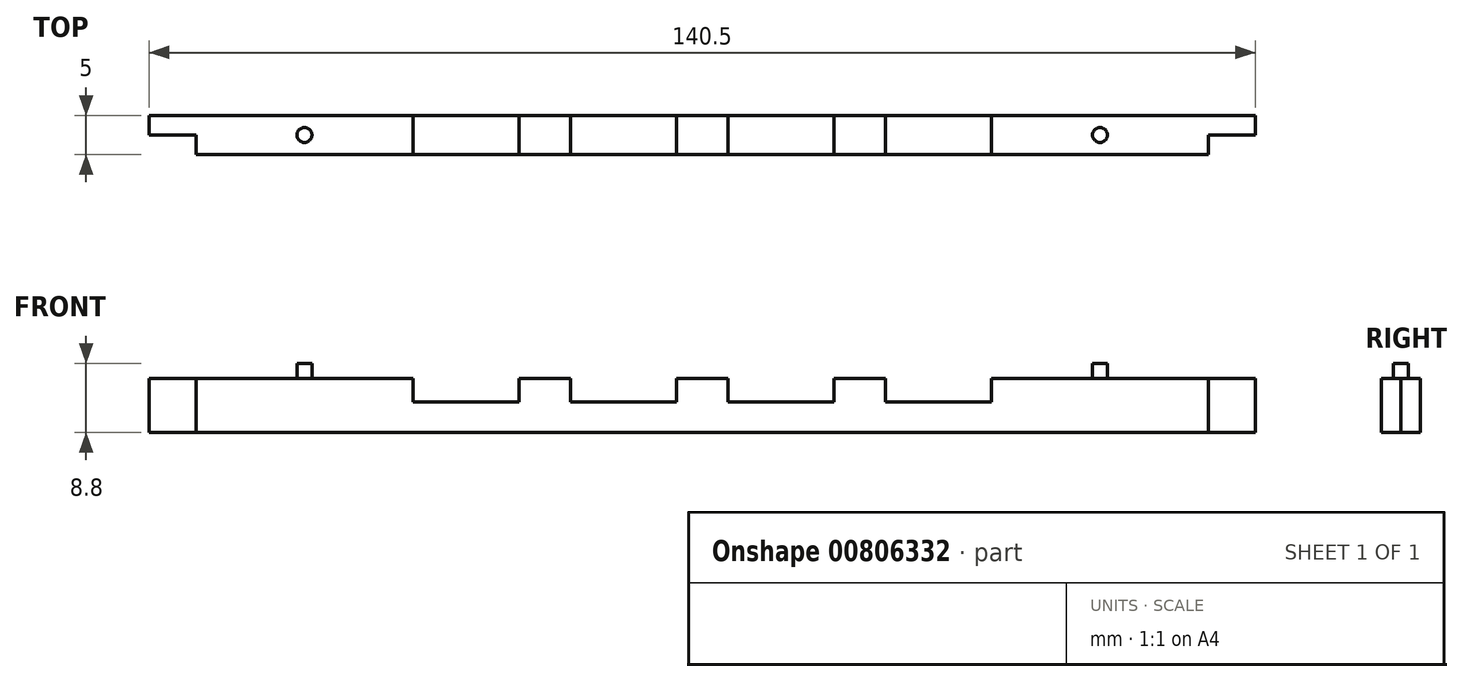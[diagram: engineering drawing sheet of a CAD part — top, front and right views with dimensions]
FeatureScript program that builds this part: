
annotation { "Feature Type Name" : "Feature", "Feature Type Description" : "" }
export const myFeature = defineFeature(function(context is Context, id is Id, definition is map)
    precondition{}
    {
        {
            var Q0;
            Q0=qCreatedBy(makeId("Front.planeOp"),FACE);
            var sketch = newSketch(context, id + "F0", { "sketchPlane" : qUnion([Q0])});
            skLineSegment(sketch, "E0.bottom", {"start": v(64.44, 6.94) * mm, "end": v(-64.16, 6.94) * mm});
            skLineSegment(sketch, "E0.top", {"start": v(64.44, -6.86) * mm, "end": v(-64.16, -6.86) * mm});
            skLineSegment(sketch, "E0.left", {"start": v(64.44, 6.94) * mm, "end": v(64.44, -6.86) * mm});
            skLineSegment(sketch, "E0.right", {"start": v(-64.16, 6.94) * mm, "end": v(-64.16, -6.86) * mm});
            skPoint(sketch, "E0.middle", {"position": v(0.14, 0.04) * mm});
            skLineSegment(sketch, "E1", {"start": v(-64.16, -6.86) * mm, "end": v(-70.1, -6.86) * mm, "construction": true});
            skLineSegment(sketch, "E2", {"start": v(64.44, -6.86) * mm, "end": v(70.4, -6.86) * mm, "construction": true});
            skLineSegment(sketch, "E3.bottom", {"start": v(-70.1, -6.86) * mm, "end": v(70.4, -6.86) * mm});
            skLineSegment(sketch, "E3.top", {"start": v(-70.1, 5.34) * mm, "end": v(70.4, 5.34) * mm});
            skLineSegment(sketch, "E3.left", {"start": v(-70.1, -6.86) * mm, "end": v(-70.1, 5.34) * mm});
            skLineSegment(sketch, "E3.right", {"start": v(70.4, -6.86) * mm, "end": v(70.4, 5.34) * mm});
            skCircle(sketch, "E4", {"center": v(65.44, 5.34) * mm, "radius": 1 * mm});
            skCircle(sketch, "E5", {"center": v(-65.16, 5.34) * mm, "radius": 1 * mm});
            skLineSegment(sketch, "E6", {"start": v(-64.16, 0.04) * mm, "end": v(64.44, 0.04) * mm, "construction": true});
            skLineSegment(sketch, "E7.bottom", {"start": v(-23.1, 3.04) * mm, "end": v(-36.6, 3.04) * mm});
            skLineSegment(sketch, "E7.top", {"start": v(-23.1, -2.96) * mm, "end": v(-36.6, -2.96) * mm});
            skLineSegment(sketch, "E7.left", {"start": v(-23.1, 3.04) * mm, "end": v(-23.1, -2.96) * mm});
            skLineSegment(sketch, "E7.right", {"start": v(-36.6, 3.04) * mm, "end": v(-36.6, -2.96) * mm});
            skPoint(sketch, "E7.middle", {"position": v(-29.86, 0.04) * mm});
            skLineSegment(sketch, "E8.bottom", {"start": v(-3.1, 3.04) * mm, "end": v(-16.6, 3.04) * mm});
            skLineSegment(sketch, "E8.top", {"start": v(-3.1, -2.96) * mm, "end": v(-16.6, -2.96) * mm});
            skLineSegment(sketch, "E8.left", {"start": v(-3.1, 3.04) * mm, "end": v(-3.1, -2.96) * mm});
            skLineSegment(sketch, "E8.right", {"start": v(-16.6, 3.04) * mm, "end": v(-16.6, -2.96) * mm});
            skPoint(sketch, "E8.middle", {"position": v(-9.86, 0.04) * mm});
            skLineSegment(sketch, "E9.bottom", {"start": v(16.9, 3.04) * mm, "end": v(3.4, 3.04) * mm});
            skLineSegment(sketch, "E9.top", {"start": v(16.9, -2.96) * mm, "end": v(3.4, -2.96) * mm});
            skLineSegment(sketch, "E9.left", {"start": v(16.9, 3.04) * mm, "end": v(16.9, -2.96) * mm});
            skLineSegment(sketch, "E9.right", {"start": v(3.4, 3.04) * mm, "end": v(3.4, -2.96) * mm});
            skPoint(sketch, "E9.middle", {"position": v(10.14, 0.04) * mm});
            skLineSegment(sketch, "E10.bottom", {"start": v(36.9, 3.04) * mm, "end": v(23.4, 3.04) * mm});
            skLineSegment(sketch, "E10.top", {"start": v(36.9, -2.96) * mm, "end": v(23.4, -2.96) * mm});
            skLineSegment(sketch, "E10.left", {"start": v(36.9, 3.04) * mm, "end": v(36.9, -2.96) * mm});
            skLineSegment(sketch, "E10.right", {"start": v(23.4, 3.04) * mm, "end": v(23.4, -2.96) * mm});
            skPoint(sketch, "E10.middle", {"position": v(30.14, 0.04) * mm});
            skPoint(sketch, "E11", {"position": v(-36.6, 0.04) * mm});
            skPoint(sketch, "E12", {"position": v(36.9, 0.04) * mm});
            skPoint(sketch, "E13", {"position": v(-70.1, 0.04) * mm});
            skPoint(sketch, "E14", {"position": v(70.4, 0.04) * mm});
            skLineSegment(sketch, "E15", {"start": v(-70.1, 0.04) * mm, "end": v(70.4, 0.04) * mm});
            skSolve(sketch);
        }
        {
            var Q0;
            {var subQ7=sQuery(id+"F0.wireOp",EDGE,"E7.top");Q0=makeQuery(id+"F0.imprint","IMPRINT",FACE,{"disambiguationData":[TD([[makeQuery(id+"F0.imprint","IMPRINT",EDGE,{"derivedFrom":subQ7}),1.0]])]});}
            extrude(context, id + "F1", {"entities" : qUnion([Q0]), "depth" : 5 * mm, "offsetDistance" : 25 * mm});
        }
        {
            var Q0;
            {var subQ0=sQuery(id+"F0.wireOp",EDGE,"E3.bottom");var subQ1=sQuery(id+"F0.wireOp",EDGE,"E0.right");var subQ2=makeQuery(id+"F0.imprint","INTERSECT",VERTEX,{"derivedFrom":[subQ1,subQ0]});Q0=makeQuery(id+"F0.imprint","IMPRINT",FACE,{"disambiguationData":[TD([[makeQuery(id+"F0.imprint","IMPRINT",EDGE,{"disambiguationData":[TD([[subQ2,1.0]])],"derivedFrom":subQ1}),-1.0]])]});}
            var Q1;
            {var subQ0=sQuery(id+"F0.wireOp",EDGE,"E3.bottom");var subQ1=sQuery(id+"F0.wireOp",EDGE,"E0.left");var subQ2=makeQuery(id+"F0.imprint","INTERSECT",VERTEX,{"derivedFrom":[subQ1,subQ0]});Q1=makeQuery(id+"F0.imprint","IMPRINT",FACE,{"disambiguationData":[TD([[makeQuery(id+"F0.imprint","IMPRINT",EDGE,{"disambiguationData":[TD([[subQ2,1.0]])],"derivedFrom":subQ1}),1.0]])]});}
            extrude(context, id + "F2", {"entities" : qUnion([Q0, Q1]), "operationType" : NewBodyOperationType.ADD, "depth" : 2.5 * mm, "offsetDistance" : 25 * mm});
        }
        {
            var Q0;
            {var subQ0=sQuery(id+"F0.wireOp",EDGE,"E15");var subQ1=sQuery(id+"F0.wireOp",EDGE,"E3.bottom");var subQ2=sQuery(id+"F0.wireOp",EDGE,"E0.right");var subQ3=sQuery(id+"F0.wireOp",EDGE,"E0.left");Q0=makeQuery(id+"F2.boolean.opBoolean","MERGE",FACE,{"derivedFrom":[makeQuery(id+"F1.opExtrude","CAP_FACE",FACE,{"disambiguationData":[OSD([subQ3,subQ2,subQ1,sQuery(id+"F0.wireOp",EDGE,"E7.top"),sQuery(id+"F0.wireOp",EDGE,"E7.left"),sQuery(id+"F0.wireOp",EDGE,"E7.right"),sQuery(id+"F0.wireOp",EDGE,"E8.top"),sQuery(id+"F0.wireOp",EDGE,"E8.left"),sQuery(id+"F0.wireOp",EDGE,"E8.right"),sQuery(id+"F0.wireOp",EDGE,"E9.top"),sQuery(id+"F0.wireOp",EDGE,"E9.left"),sQuery(id+"F0.wireOp",EDGE,"E9.right"),sQuery(id+"F0.wireOp",EDGE,"E10.top"),sQuery(id+"F0.wireOp",EDGE,"E10.left"),sQuery(id+"F0.wireOp",EDGE,"E10.right"),subQ0])],"isStart":true}),makeQuery(id+"F2.opExtrude","CAP_FACE",FACE,{"disambiguationData":[OSD([subQ3,subQ1,sQuery(id+"F0.wireOp",EDGE,"E3.right"),subQ0])],"isStart":true}),makeQuery(id+"F2.opExtrude","CAP_FACE",FACE,{"disambiguationData":[OSD([subQ2,subQ1,sQuery(id+"F0.wireOp",EDGE,"E3.left"),subQ0])],"isStart":true})]});}
            var sketch = newSketch(context, id + "F3", { "sketchPlane" : qUnion([Q0])});
            skPoint(sketch, "E16", {"position": v(-41.9, 0.04) * mm});
            skPoint(sketch, "E17", {"position": v(41.6, 0.04) * mm});
            skLineSegment(sketch, "E18.bottom", {"start": v(-41.9, 0.04) * mm, "end": v(41.68, 0.04) * mm});
            skLineSegment(sketch, "E18.top", {"start": v(-41.9, -6.86) * mm, "end": v(41.68, -6.86) * mm});
            skLineSegment(sketch, "E18.left", {"start": v(-41.9, 0.04) * mm, "end": v(-41.9, -6.86) * mm});
            skLineSegment(sketch, "E18.right", {"start": v(41.68, 0.04) * mm, "end": v(41.68, -6.86) * mm});
            skSolve(sketch);
        }
        {
            var Q0;
            {var subQ0=sQuery(id+"F0.wireOp",EDGE,"E15");var subQ1=makeQuery(id+"F0.imprint","INTERSECT",VERTEX,{"derivedFrom":[sQuery(id+"F0.wireOp",EDGE,"E0.left"),subQ0]});Q0=makeQuery(id+"F2.boolean.opBoolean","MERGE",FACE,{"derivedFrom":[makeQuery(id+"F1.opExtrude","SWEPT_FACE",FACE,{"disambiguationData":[OSD([subQ0]),TDD([makeQuery(id+"F0.imprint","IMPRINT",EDGE,{"disambiguationData":[TD([[subQ1,1.0]])],"derivedFrom":subQ0})])]}),makeQuery(id+"F2.opExtrude","SWEPT_FACE",FACE,{"disambiguationData":[OSD([subQ0]),TDD([makeQuery(id+"F0.imprint","IMPRINT",EDGE,{"disambiguationData":[TD([[makeQuery(id+"F0.imprint","INTERSECT",VERTEX,{"derivedFrom":[sQuery(id+"F0.wireOp",EDGE,"E3.right"),subQ0]}),1.0]])],"derivedFrom":subQ0})])]})]});}
            var sketch = newSketch(context, id + "F4", { "sketchPlane" : qUnion([Q0])});
            skLineSegment(sketch, "E19", {"start": v(50.67, -5) * mm, "end": v(50.67, 0) * mm, "construction": true});
            skPoint(sketch, "E20", {"position": v(50.67, -2.5) * mm});
            skCircle(sketch, "E21", {"center": v(50.67, -2.5) * mm, "radius": 0.95 * mm});
            skSolve(sketch);
        }
        {
            var Q0;
            {var subQ0=sQuery(id+"F0.wireOp",EDGE,"E15");var subQ1=makeQuery(id+"F0.imprint","INTERSECT",VERTEX,{"derivedFrom":[sQuery(id+"F0.wireOp",EDGE,"E0.right"),subQ0]});Q0=makeQuery(id+"F2.boolean.opBoolean","MERGE",FACE,{"derivedFrom":[makeQuery(id+"F1.opExtrude","SWEPT_FACE",FACE,{"disambiguationData":[OSD([subQ0]),TDD([makeQuery(id+"F0.imprint","IMPRINT",EDGE,{"disambiguationData":[TD([[subQ1,-1.0]])],"derivedFrom":subQ0})])]}),makeQuery(id+"F2.opExtrude","SWEPT_FACE",FACE,{"disambiguationData":[OSD([subQ0]),TDD([makeQuery(id+"F0.imprint","IMPRINT",EDGE,{"disambiguationData":[TD([[makeQuery(id+"F0.imprint","INTERSECT",VERTEX,{"derivedFrom":[sQuery(id+"F0.wireOp",EDGE,"E3.left"),subQ0]}),-1.0]])],"derivedFrom":subQ0})])]})]});}
            var sketch = newSketch(context, id + "F5", { "sketchPlane" : qUnion([Q0])});
            skLineSegment(sketch, "E22", {"start": v(-50.38, -5) * mm, "end": v(-50.38, 0) * mm, "construction": true});
            skPoint(sketch, "E23", {"position": v(-50.38, -2.5) * mm});
            skCircle(sketch, "E24", {"center": v(-50.38, -2.5) * mm, "radius": 0.95 * mm});
            skSolve(sketch);
        }
        {
            var Q0;
            Q0=makeQuery(id+"F5.imprint","IMPRINT",FACE,{"disambiguationData":[TD([[makeQuery(id+"F5.imprint","IMPRINT",EDGE,{"derivedFrom":sQuery(id+"F5.wireOp",EDGE,"E24")}),1.0]])]});
            extrude(context, id + "F6", {"entities" : qUnion([Q0]), "operationType" : NewBodyOperationType.ADD, "depth" : 1.9 * mm, "offsetDistance" : 25 * mm});
        }
        {
            var Q0;
            Q0=qSketchRegion(id+"F4",true);
            extrude(context, id + "F7", {"entities" : qUnion([Q0]), "operationType" : NewBodyOperationType.ADD, "depth" : 1.9 * mm, "offsetDistance" : 25 * mm});
        }
    });
